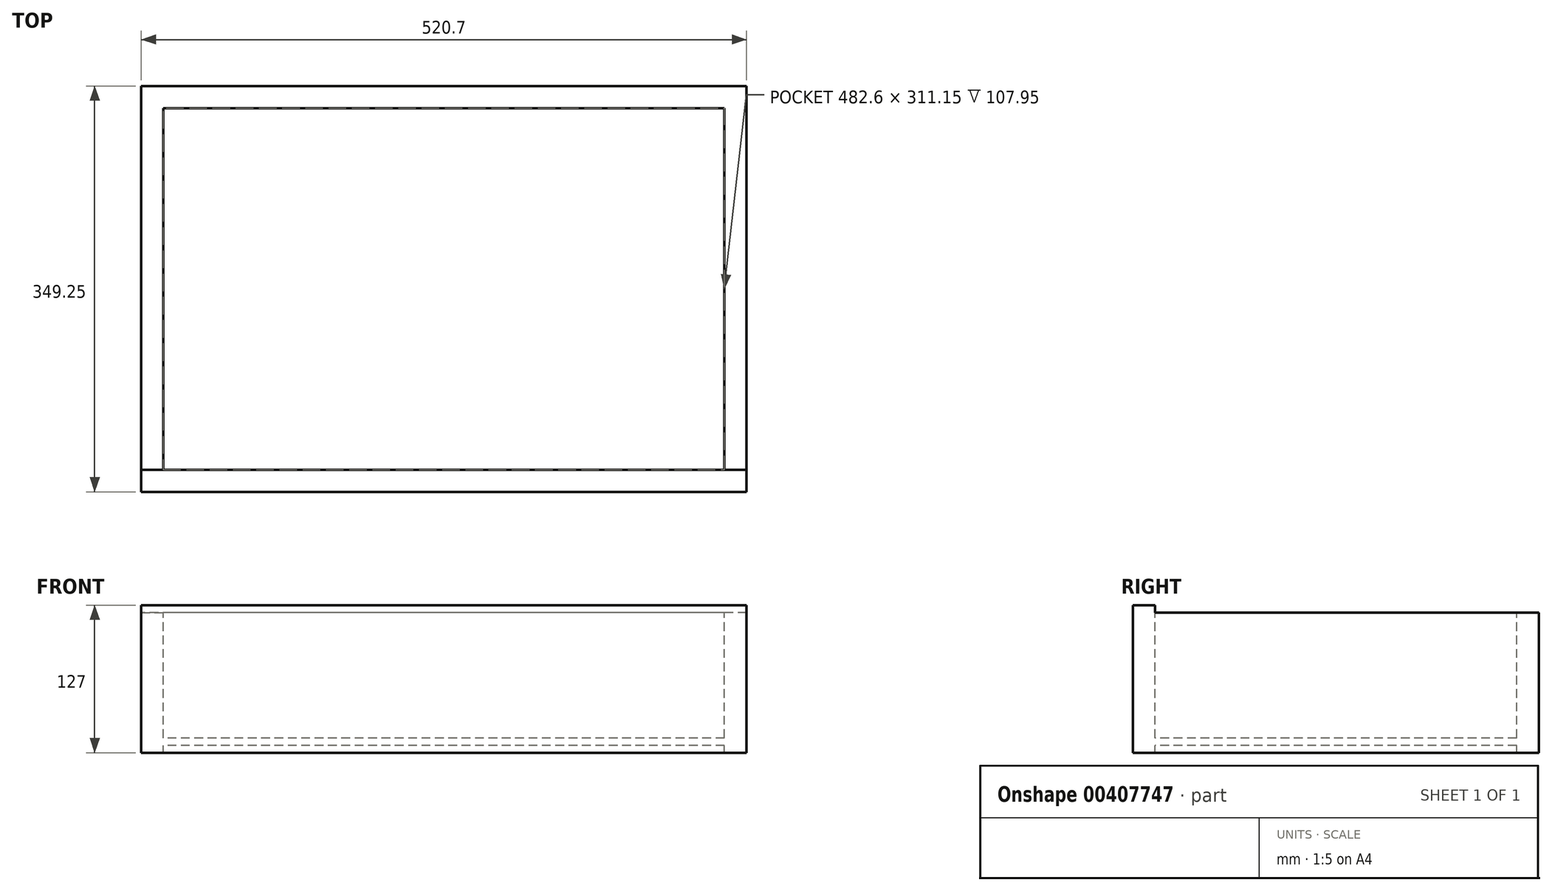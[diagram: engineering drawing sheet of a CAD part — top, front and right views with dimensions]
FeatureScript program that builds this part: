
annotation { "Feature Type Name" : "Feature", "Feature Type Description" : "" }
export const myFeature = defineFeature(function(context is Context, id is Id, definition is map)
    precondition{}
    {
        {
            var Q0;
            Q0=qCreatedBy(makeId("Front.planeOp"),FACE);
            var sketch = newSketch(context, id + "F0", { "sketchPlane" : qUnion([Q0])});
            skLineSegment(sketch, "E0.bottom", {"start": v(260.35, 63.5) * mm, "end": v(-260.35, 63.5) * mm});
            skLineSegment(sketch, "E0.top", {"start": v(260.35, -63.5) * mm, "end": v(-260.35, -63.5) * mm});
            skLineSegment(sketch, "E0.left", {"start": v(260.35, 63.5) * mm, "end": v(260.35, -63.5) * mm});
            skLineSegment(sketch, "E0.right", {"start": v(-260.35, 63.5) * mm, "end": v(-260.35, -63.5) * mm});
            skPoint(sketch, "E0.middle", {"position": v(0, 0) * mm});
            skSolve(sketch);
        }
        {
            var Q0;
            Q0=makeQuery(id+"F0.imprint","IMPRINT",FACE,{"disambiguationData":[TD([[makeQuery(id+"F0.imprint","IMPRINT",EDGE,{"derivedFrom":sQuery(id+"F0.wireOp",EDGE,"E0.bottom")}),1.0]])]});
            extrude(context, id + "F1", {"entities" : qUnion([Q0]), "oppositeDirection" : true, "depth" : 19.05 * mm});
        }
        {
            var Q0;
            Q0=makeQuery(id+"F1.opExtrude","CAP_FACE",FACE,{"disambiguationData":[OSD([sQuery(id+"F0.wireOp",EDGE,"E0.bottom"),sQuery(id+"F0.wireOp",EDGE,"E0.top"),sQuery(id+"F0.wireOp",EDGE,"E0.left"),sQuery(id+"F0.wireOp",EDGE,"E0.right")])],"isStart":false});
            var sketch = newSketch(context, id + "F2", { "sketchPlane" : qUnion([Q0])});
            skLineSegment(sketch, "E1.bottom", {"start": v(-260.35, -63.5) * mm, "end": v(-241.3, -63.5) * mm});
            skLineSegment(sketch, "E1.top", {"start": v(-260.35, 57.15) * mm, "end": v(-241.3, 57.15) * mm});
            skLineSegment(sketch, "E1.left", {"start": v(-260.35, -63.5) * mm, "end": v(-260.35, 57.15) * mm});
            skLineSegment(sketch, "E1.right", {"start": v(-241.3, -63.5) * mm, "end": v(-241.3, -57.15) * mm});
            skLineSegment(sketch, "E2", {"start": v(-241.3, -50.8) * mm, "end": v(-250.83, -50.8) * mm});
            skLineSegment(sketch, "E3", {"start": v(-250.83, -50.8) * mm, "end": v(-250.83, -57.15) * mm});
            skLineSegment(sketch, "E4", {"start": v(-250.83, -57.15) * mm, "end": v(-241.3, -57.15) * mm});
            skLineSegment(sketch, "E5.trimOffspring", {"start": v(-241.3, -50.8) * mm, "end": v(-241.3, 57.15) * mm});
            skSolve(sketch);
        }
        {
            var Q0;
            Q0 = qSketchRegion(id + "F2", true);
            extrude(context, id + "F3", {"entities" : qUnion([Q0]), "operationType" : NewBodyOperationType.ADD, "depth" : 311.15 * mm});
        }
        {
            var Q0;
            Q0=makeQuery(id+"F1.opExtrude","SWEPT_BODY",BODY,{"disambiguationData":[OSD([sQuery(id+"F0.wireOp",EDGE,"E0.bottom"),sQuery(id+"F0.wireOp",EDGE,"E0.top"),sQuery(id+"F0.wireOp",EDGE,"E0.left"),sQuery(id+"F0.wireOp",EDGE,"E0.right")])]});
            var Q1;
            Q1=qCreatedBy(makeId("Right.planeOp"),FACE);
            mirror(context, id + "F4", {"operationType" : NewBodyOperationType.ADD, "entities" : qUnion([Q0]), "mirrorPlane" : qUnion([Q1])});
        }
        {
            var Q0;
            Q0=makeQuery(id+"F3.opExtrude","CAP_FACE",FACE,{"disambiguationData":[OSD([sQuery(id+"F2.wireOp",EDGE,"E1.bottom"),sQuery(id+"F2.wireOp",EDGE,"E1.top"),sQuery(id+"F2.wireOp",EDGE,"E1.left"),sQuery(id+"F2.wireOp",EDGE,"E1.right")])],"isStart":false});
            var sketch = newSketch(context, id + "F5", { "sketchPlane" : qUnion([Q0])});
            skLineSegment(sketch, "E6.bottom", {"start": v(-260.35, 57.15) * mm, "end": v(260.35, 57.15) * mm});
            skLineSegment(sketch, "E6.top", {"start": v(-260.35, -63.5) * mm, "end": v(260.35, -63.5) * mm});
            skLineSegment(sketch, "E6.left", {"start": v(-260.35, 57.15) * mm, "end": v(-260.35, -63.5) * mm});
            skLineSegment(sketch, "E6.right", {"start": v(260.35, 57.15) * mm, "end": v(260.35, -63.5) * mm});
            skSolve(sketch);
        }
        {
            var Q0;
            Q0 = qSketchRegion(id + "F5", true);
            extrude(context, id + "F6", {"entities" : qUnion([Q0]), "operationType" : NewBodyOperationType.ADD, "depth" : 19.05 * mm});
        }
        {
            var Q0;
            Q0=makeQuery(id+"F6.opExtrude","CAP_FACE",FACE,{"disambiguationData":[OSD([sQuery(id+"F5.wireOp",EDGE,"E6.bottom"),sQuery(id+"F5.wireOp",EDGE,"E6.top"),sQuery(id+"F5.wireOp",EDGE,"E6.left"),sQuery(id+"F5.wireOp",EDGE,"E6.right")])],"isStart":true});
            var sketch = newSketch(context, id + "F7", { "sketchPlane" : qUnion([Q0])});
            skLineSegment(sketch, "E7.bottom", {"start": v(-250.83, -50.8) * mm, "end": v(250.83, -50.8) * mm});
            skLineSegment(sketch, "E7.top", {"start": v(-250.83, -57.15) * mm, "end": v(250.83, -57.15) * mm});
            skLineSegment(sketch, "E7.left", {"start": v(-250.83, -50.8) * mm, "end": v(-250.83, -57.15) * mm});
            skLineSegment(sketch, "E7.right", {"start": v(250.83, -50.8) * mm, "end": v(250.83, -57.15) * mm});
            skSolve(sketch);
        }
        {
            var Q0;
            Q0 = qSketchRegion(id + "F7", true);
            extrude(context, id + "F8", {"entities" : qUnion([Q0]), "operationType" : NewBodyOperationType.REMOVE, "oppositeDirection" : true, "depth" : 6.35 * mm});
        }
        {
            var Q0;
            Q0=makeQuery(id+"F1.opExtrude","CAP_FACE",FACE,{"disambiguationData":[OSD([sQuery(id+"F0.wireOp",EDGE,"E0.bottom"),sQuery(id+"F0.wireOp",EDGE,"E0.top"),sQuery(id+"F0.wireOp",EDGE,"E0.left"),sQuery(id+"F0.wireOp",EDGE,"E0.right")])],"isStart":false});
            var sketch = newSketch(context, id + "F9", { "sketchPlane" : qUnion([Q0])});
            skLineSegment(sketch, "E8.bottom", {"start": v(-250.83, -50.8) * mm, "end": v(250.83, -50.8) * mm});
            skLineSegment(sketch, "E8.top", {"start": v(-250.83, -57.15) * mm, "end": v(250.83, -57.15) * mm});
            skLineSegment(sketch, "E8.left", {"start": v(-250.83, -50.8) * mm, "end": v(-250.83, -57.15) * mm});
            skLineSegment(sketch, "E8.right", {"start": v(250.83, -50.8) * mm, "end": v(250.83, -57.15) * mm});
            skSolve(sketch);
        }
        {
            var Q0;
            Q0 = qSketchRegion(id + "F9", true);
            var Q1;
            Q1=makeQuery(id+"F8.boolean.opBoolean","COPY",FACE,{"derivedFrom":makeQuery(id+"F8.opExtrude","CAP_FACE",FACE,{"disambiguationData":[OSD([sQuery(id+"F7.wireOp",EDGE,"E7.bottom"),sQuery(id+"F7.wireOp",EDGE,"E7.top"),sQuery(id+"F7.wireOp",EDGE,"E7.left"),sQuery(id+"F7.wireOp",EDGE,"E7.right")])],"isStart":false})});
            extrude(context, id + "F10", {"entities" : qUnion([Q0]), "operationType" : NewBodyOperationType.ADD, "endBound" : BoundingType.UP_TO_SURFACE, "endBoundEntityFace" : qUnion([Q1]), "depth" : 25.4 * mm});
        }
    });
